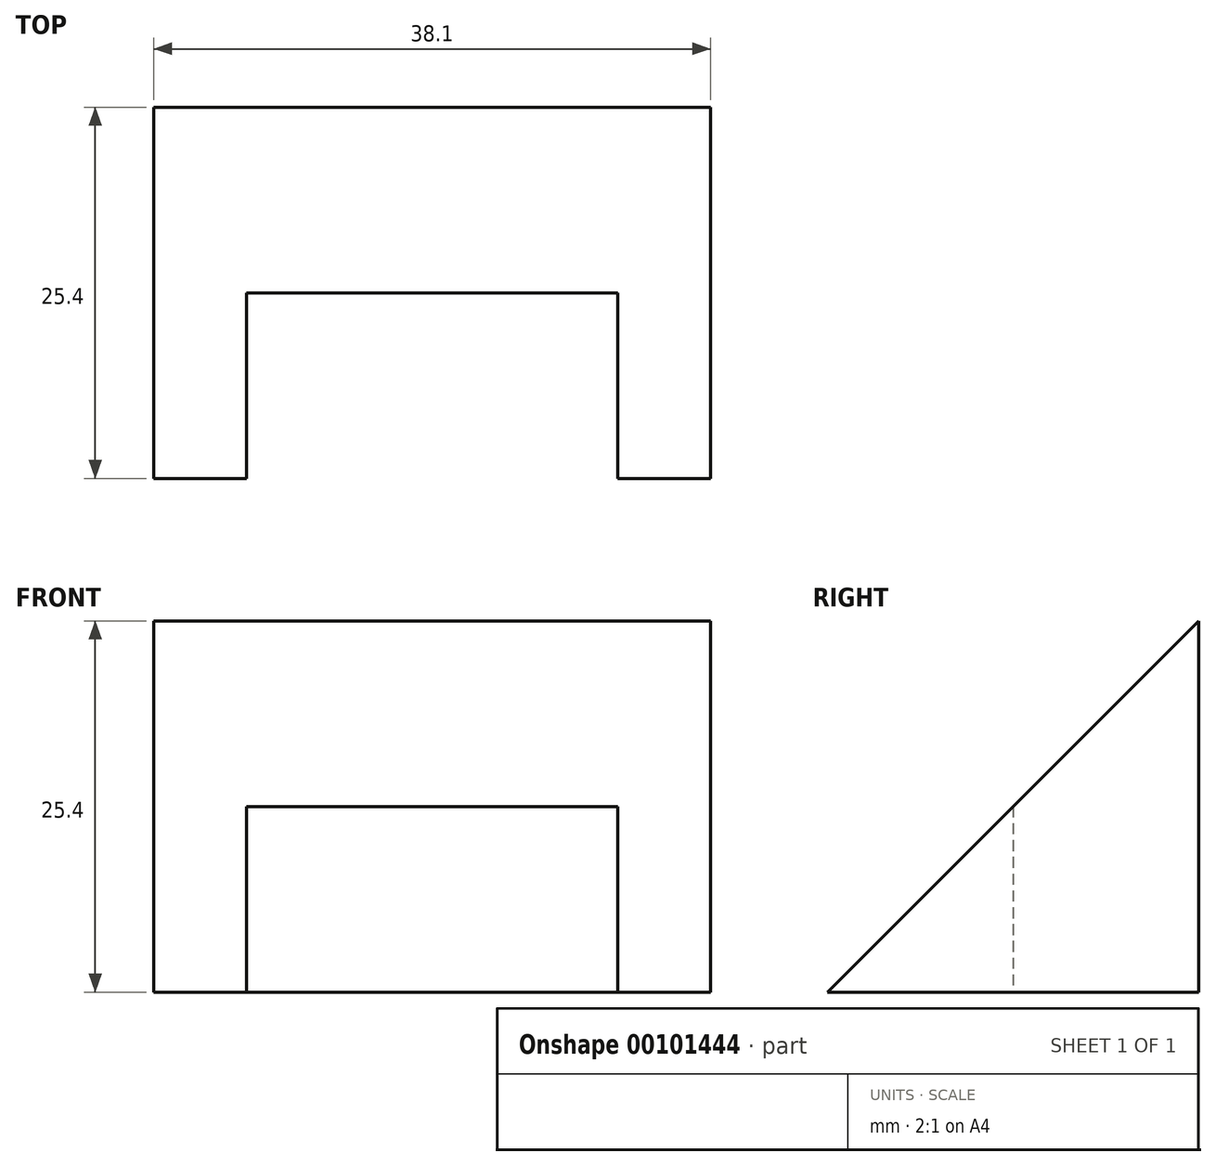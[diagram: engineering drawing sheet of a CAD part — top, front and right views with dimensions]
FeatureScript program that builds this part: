
annotation { "Feature Type Name" : "Feature", "Feature Type Description" : "" }
export const myFeature = defineFeature(function(context is Context, id is Id, definition is map)
    precondition{}
    {
        {
            var Q0;
            Q0=qCreatedBy(makeId("Front.planeOp"),FACE);
            var sketch = newSketch(context, id + "F0", { "sketchPlane" : qUnion([Q0])});
            skLineSegment(sketch, "E0", {"start": v(0, 0) * mm, "end": v(38.1, 0) * mm});
            skLineSegment(sketch, "E1", {"start": v(38.1, 0) * mm, "end": v(38.1, 25.4) * mm});
            skLineSegment(sketch, "E2", {"start": v(38.1, 25.4) * mm, "end": v(0, 25.4) * mm});
            skLineSegment(sketch, "E3", {"start": v(0, 25.4) * mm, "end": v(0, 0) * mm});
            skSolve(sketch);
        }
        {
            var Q0;
            Q0 = qSketchRegion(id + "F0", true);
            extrude(context, id + "F1", {"entities" : qUnion([Q0]), "oppositeDirection" : true, "depth" : 25.4 * mm});
        }
        {
            var Q0;
            Q0=makeQuery(id+"F1.opExtrude","SWEPT_FACE",FACE,{"disambiguationData":[OSD([sQuery(id+"F0.wireOp",EDGE,"E1")])]});
            var sketch = newSketch(context, id + "F2", { "sketchPlane" : qUnion([Q0])});
            skLineSegment(sketch, "E4", {"start": v(25.4, 25.4) * mm, "end": v(0, 0) * mm});
            skLineSegment(sketch, "E5", {"start": v(0, 0) * mm, "end": v(0, 25.4) * mm});
            skLineSegment(sketch, "E6", {"start": v(0, 25.4) * mm, "end": v(25.4, 25.4) * mm});
            skSolve(sketch);
        }
        {
            var Q0;
            Q0 = qSketchRegion(id + "F2", true);
            extrude(context, id + "F3", {"entities" : qUnion([Q0]), "operationType" : NewBodyOperationType.REMOVE, "oppositeDirection" : true, "depth" : 38.1 * mm});
        }
        {
            var Q0;
            Q0=makeQuery(id+"F1.opExtrude","SWEPT_FACE",FACE,{"disambiguationData":[OSD([sQuery(id+"F0.wireOp",EDGE,"E0")])]});
            var sketch = newSketch(context, id + "F4", { "sketchPlane" : qUnion([Q0])});
            skLineSegment(sketch, "E7", {"start": v(19.05, 0) * mm, "end": v(6.35, 0) * mm});
            skLineSegment(sketch, "E8", {"start": v(6.35, 0) * mm, "end": v(6.35, -12.7) * mm});
            skLineSegment(sketch, "E9", {"start": v(6.35, -12.7) * mm, "end": v(31.75, -12.7) * mm});
            skLineSegment(sketch, "E10", {"start": v(31.75, -12.7) * mm, "end": v(31.75, 0) * mm});
            skLineSegment(sketch, "E11", {"start": v(31.75, 0) * mm, "end": v(19.05, 0) * mm});
            skSolve(sketch);
        }
        {
            var Q0;
            Q0 = qSketchRegion(id + "F4", true);
            extrude(context, id + "F5", {"entities" : qUnion([Q0]), "operationType" : NewBodyOperationType.REMOVE, "oppositeDirection" : true, "depth" : 25.4 * mm});
        }
    });
